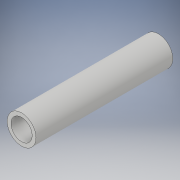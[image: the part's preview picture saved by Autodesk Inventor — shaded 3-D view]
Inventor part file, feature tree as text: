
AUTODESK INVENTOR PART (.ipt)
format: ipt  version: 2019 (Build 230136000, 136)  size: 98,304 bytes
history: native  units: mm
features: extrude x2, sketch x2
ambient origin geometry x8: Origin, YZ Plane, XZ Plane, XY Plane, X Axis, Y Axis, Z Axis, Center Point
bodies: Solid1 (feature_tree)
feature tree (4):
  extrude  "Extrusion1"  Depth=71.05mm TaperAngle=0.0deg
  extrude  "Extrusion2"  Depth=71.05mm TaperAngle=0.0deg
  sketch  "Sketch1"  dims[d0=15.0mm d1=71.05mm d2=0.0mm]
  sketch  "Sketch2"  dims[d3=11.0mm d4=71.05mm d5=0.0mm]
